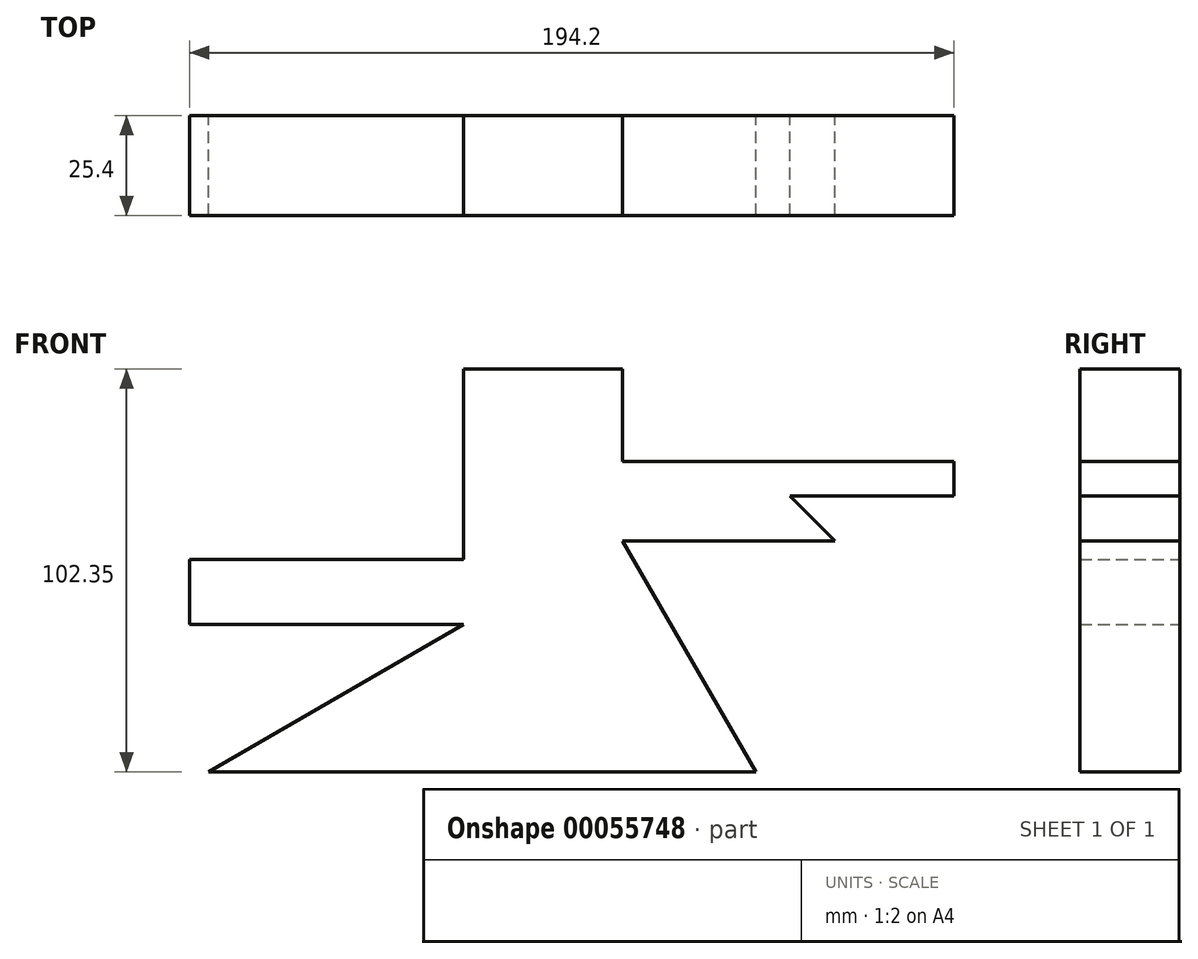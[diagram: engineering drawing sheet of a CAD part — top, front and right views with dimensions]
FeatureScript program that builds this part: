
annotation { "Feature Type Name" : "Feature", "Feature Type Description" : "" }
export const myFeature = defineFeature(function(context is Context, id is Id, definition is map)
    precondition{}
    {
        {
            var Q0;
            Q0=qCreatedBy(makeId("Front.planeOp"),FACE);
            var sketch = newSketch(context, id + "F0", { "sketchPlane" : qUnion([Q0])});
            skLineSegment(sketch, "E0", {"start": v(-92.28, -61.17) * mm, "end": v(-27.44, -23.74) * mm});
            skLineSegment(sketch, "E1", {"start": v(-27.44, -7.17) * mm, "end": v(-27.44, 41.18) * mm});
            skLineSegment(sketch, "E2", {"start": v(-27.44, 41.18) * mm, "end": v(12.88, 41.18) * mm});
            skLineSegment(sketch, "E3", {"start": v(12.88, 17.64) * mm, "end": v(46.76, 17.64) * mm});
            skLineSegment(sketch, "E4", {"start": v(12.88, 41.18) * mm, "end": v(12.88, 17.64) * mm});
            skLineSegment(sketch, "E5", {"start": v(-92.28, -61.17) * mm, "end": v(46.76, -61.17) * mm});
            skLineSegment(sketch, "E6", {"start": v(46.76, -61.17) * mm, "end": v(12.88, -2.48) * mm});
            skLineSegment(sketch, "E7", {"start": v(12.88, -2.48) * mm, "end": v(66.88, -2.48) * mm});
            skLineSegment(sketch, "E8", {"start": v(66.88, -2.48) * mm, "end": v(55.4, 8.99) * mm});
            skLineSegment(sketch, "E9.bottom", {"start": v(46.76, 17.64) * mm, "end": v(97.1, 17.64) * mm});
            skLineSegment(sketch, "E9.top", {"start": v(55.4, 8.99) * mm, "end": v(97.1, 8.99) * mm});
            skLineSegment(sketch, "E9.right", {"start": v(97.1, 17.64) * mm, "end": v(97.1, 8.99) * mm});
            skLineSegment(sketch, "E10.bottom", {"start": v(-27.44, -23.74) * mm, "end": v(-97.1, -23.74) * mm});
            skLineSegment(sketch, "E10.top", {"start": v(-27.44, -7.17) * mm, "end": v(-97.1, -7.17) * mm});
            skLineSegment(sketch, "E10.right", {"start": v(-97.1, -23.74) * mm, "end": v(-97.1, -7.17) * mm});
            skSolve(sketch);
        }
        {
            var Q0;
            Q0 = qSketchRegion(id + "F0", true);
            extrude(context, id + "F1", {"entities" : qUnion([Q0]), "depth" : 25.4 * mm});
        }
    });
